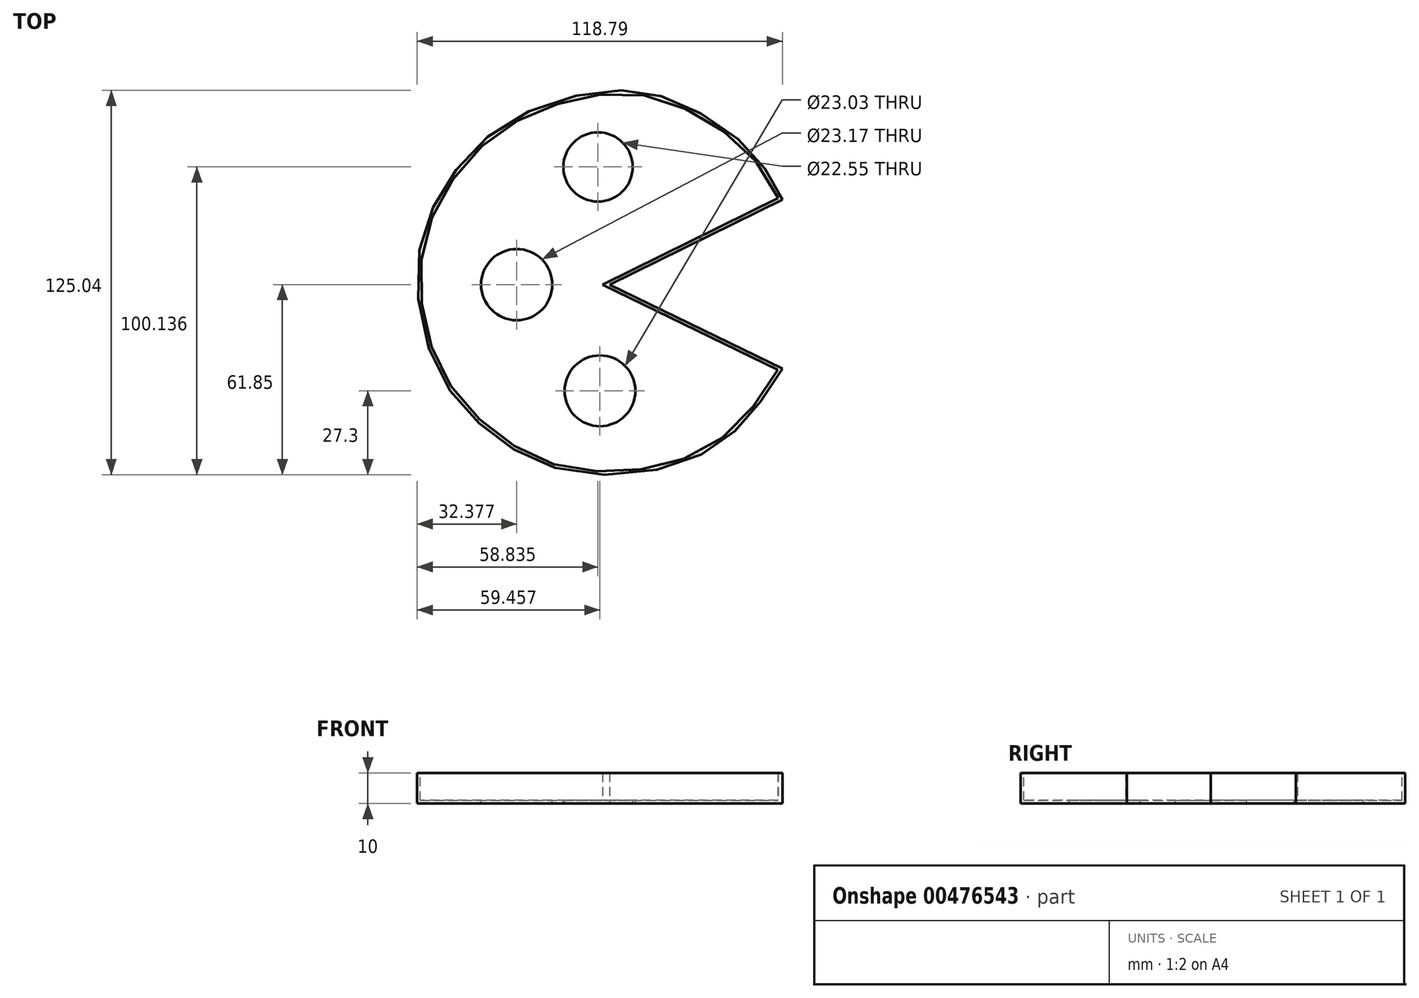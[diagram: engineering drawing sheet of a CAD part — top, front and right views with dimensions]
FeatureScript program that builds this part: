
annotation { "Feature Type Name" : "Feature", "Feature Type Description" : "" }
export const myFeature = defineFeature(function(context is Context, id is Id, definition is map)
    precondition{}
    {
        {
            var Q0;
            Q0=qCreatedBy(makeId("Top.planeOp"),FACE);
            var sketch = newSketch(context, id + "F0", { "sketchPlane" : qUnion([Q0])});
            skLineSegment(sketch, "E0", {"start": v(56.22, 27.67) * mm, "end": v(56.02, 27.26) * mm});
            skLineSegment(sketch, "E1", {"start": v(56.22, 27.67) * mm, "end": v(0, 0) * mm});
            skLineSegment(sketch, "E2", {"start": v(56.22, -27.36) * mm, "end": v(0, 0) * mm});
            skFitSpline(sketch, "E3", {"points": [v(56.22, 27.67) * mm, v(46.05, 43.35) * mm, v(23.06, 59.05) * mm, v(0, 63.07) * mm, v(-31.7, 53.57) * mm, v(-52.87, 33.13) * mm, v(-62.36, 6.85) * mm, v(-56.15, -27.1) * mm, v(-38.63, -48.27) * mm, v(-13.45, -60.68) * mm, v(23.06, -58.12) * mm, v(43.5, -44.98) * mm, v(56.22, -27.36) * mm], "startDerivative": vector(-117.85, 231.35) * mm, "endDerivative": vector(157.27, 250.07) * mm});
            skSolve(sketch);
        }
        {
            var Q0;
            Q0=makeQuery(id+"F0.imprint","IMPRINT",FACE,{"disambiguationData":[TD([[makeQuery(id+"F0.imprint","IMPRINT",EDGE,{"derivedFrom":sQuery(id+"F0.wireOp",EDGE,"E1")}),-1.0]])]});
            extrude(context, id + "F1", {"entities" : qUnion([Q0]), "depth" : 10 * mm});
        }
        {
            var Q0;
            Q0=makeQuery(id+"F1.opExtrude","CAP_FACE",FACE,{"disambiguationData":[OSD([sQuery(id+"F0.wireOp",EDGE,"E1"),sQuery(id+"F0.wireOp",EDGE,"E2"),sQuery(id+"F0.wireOp",EDGE,"E3")])],"isStart":false});
            shell(context, id + "F2", {"entities" : qUnion([Q0]), "thickness" : 1 * mm});
        }
        {
            var Q0;
            Q0=makeQuery(id+"F2.opShell","OFFSET_FACE",FACE,{"disambiguationData":[OSD([sQuery(id+"F0.wireOp",EDGE,"E1"),sQuery(id+"F0.wireOp",EDGE,"E2"),sQuery(id+"F0.wireOp",EDGE,"E3")])]});
            var sketch = newSketch(context, id + "F3", { "sketchPlane" : qUnion([Q0])});
            skCircle(sketch, "E4", {"center": v(-3.74, 38.29) * mm, "radius": 11.27 * mm});
            skCircle(sketch, "E5", {"center": v(-30.2, 0) * mm, "radius": 11.58 * mm});
            skCircle(sketch, "E6", {"center": v(-3.11, -34.55) * mm, "radius": 11.52 * mm});
            skSolve(sketch);
        }
        {
            var Q0;
            Q0=makeQuery(id+"F3.imprint","IMPRINT",FACE,{"disambiguationData":[TD([[makeQuery(id+"F3.imprint","IMPRINT",EDGE,{"derivedFrom":sQuery(id+"F3.wireOp",EDGE,"E4")}),1.0]])]});
            var Q1;
            Q1=makeQuery(id+"F3.imprint","IMPRINT",FACE,{"disambiguationData":[TD([[makeQuery(id+"F3.imprint","IMPRINT",EDGE,{"derivedFrom":sQuery(id+"F3.wireOp",EDGE,"E5")}),1.0]])]});
            var Q2;
            Q2=makeQuery(id+"F3.imprint","IMPRINT",FACE,{"disambiguationData":[TD([[makeQuery(id+"F3.imprint","IMPRINT",EDGE,{"derivedFrom":sQuery(id+"F3.wireOp",EDGE,"E6")}),1.0]])]});
            extrude(context, id + "F4", {"entities" : qUnion([Q0, Q1, Q2]), "operationType" : NewBodyOperationType.REMOVE, "oppositeDirection" : true, "depth" : 25 * mm});
        }
    });
